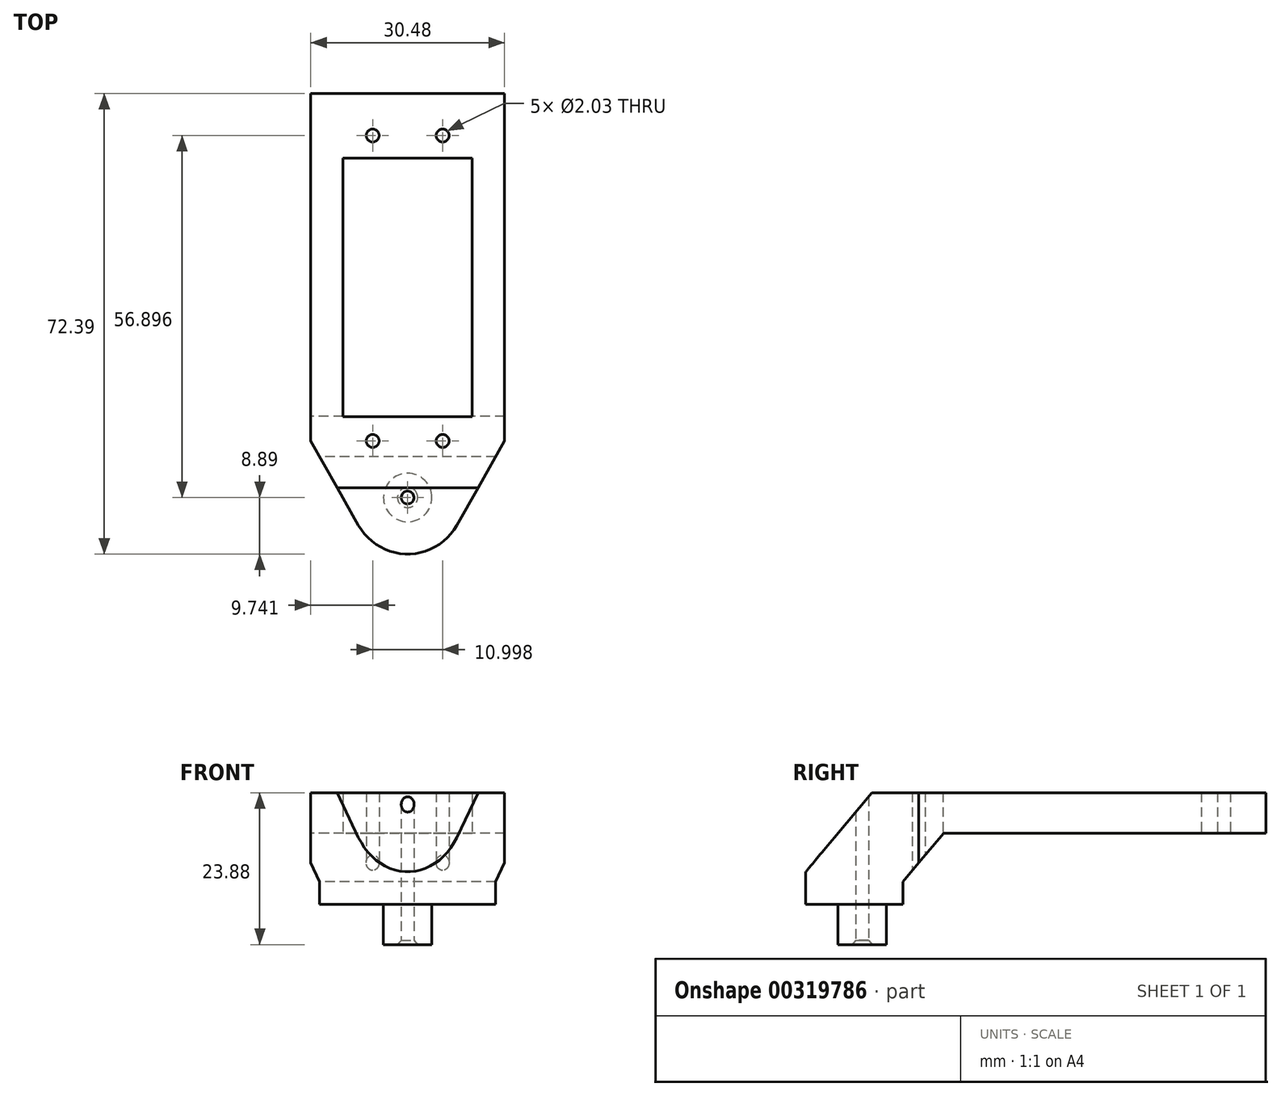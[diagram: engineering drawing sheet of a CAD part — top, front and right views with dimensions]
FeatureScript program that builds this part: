
annotation { "Feature Type Name" : "Feature", "Feature Type Description" : "" }
export const myFeature = defineFeature(function(context is Context, id is Id, definition is map)
    precondition{}
    {
        {
            var Q0;
            Q0=qCreatedBy(makeId("Top.planeOp"),FACE);
            var sketch = newSketch(context, id + "F0", { "sketchPlane" : qUnion([Q0])});
            skLineSegment(sketch, "E0", {"start": v(0, -10.16) * mm, "end": v(-10.16, -10.16) * mm});
            skLineSegment(sketch, "E1", {"start": v(-10.16, -10.16) * mm, "end": v(-10.16, 30.48) * mm});
            skLineSegment(sketch, "E2", {"start": v(-10.16, 30.48) * mm, "end": v(0, 30.48) * mm});
            skLineSegment(sketch, "E3", {"start": v(0, 40.64) * mm, "end": v(-15.24, 40.64) * mm});
            skLineSegment(sketch, "E4", {"start": v(-15.24, 40.64) * mm, "end": v(-15.24, -13.97) * mm});
            skLineSegment(sketch, "E5", {"start": v(-15.24, -13.97) * mm, "end": v(0, -13.97) * mm, "construction": true});
            skPoint(sketch, "E6", {"position": v(-5.5, -13.97) * mm});
            skCircle(sketch, "E7", {"center": v(0, 0) * mm, "radius": 6.35 * mm, "construction": true});
            skCircle(sketch, "E8", {"center": v(-5.5, -13.97) * mm, "radius": 1.02 * mm});
            skCircle(sketch, "E9", {"center": v(0, -22.86) * mm, "radius": 3.81 * mm, "construction": true});
            skCircle(sketch, "E10", {"center": v(-5.5, 34.04) * mm, "radius": 1.02 * mm});
            skCircle(sketch, "E11.MirrorC", {"center": v(5.5, -13.97) * mm, "radius": 1.02 * mm});
            skCircle(sketch, "E12.MirrorC", {"center": v(5.5, 34.04) * mm, "radius": 1.02 * mm});
            skLineSegment(sketch, "E13.MirrorCS", {"start": v(15.24, -13.97) * mm, "end": v(0, -13.97) * mm, "construction": true});
            skLineSegment(sketch, "E14.MirrorCS", {"start": v(15.24, 40.64) * mm, "end": v(15.24, -13.97) * mm});
            skLineSegment(sketch, "E15.MirrorCS", {"start": v(0, -10.16) * mm, "end": v(10.16, -10.16) * mm});
            skLineSegment(sketch, "E16.MirrorCS", {"start": v(10.16, 30.48) * mm, "end": v(0, 30.48) * mm});
            skLineSegment(sketch, "E17.MirrorCS", {"start": v(10.16, -10.16) * mm, "end": v(10.16, 30.48) * mm});
            skLineSegment(sketch, "E18.MirrorCS", {"start": v(0, 40.64) * mm, "end": v(15.24, 40.64) * mm});
            skCircle(sketch, "E19", {"center": v(0, -22.86) * mm, "radius": 8.9 * mm});
            skLineSegment(sketch, "E20", {"start": v(-15.24, -13.97) * mm, "end": v(-7.74, -27.24) * mm});
            skLineSegment(sketch, "E21", {"start": v(15.24, -13.97) * mm, "end": v(7.74, -27.24) * mm});
            skSolve(sketch);
        }
        {
            var Q0;
            Q0 = qSketchRegion(id + "F0", true);
            extrude(context, id + "F1", {"entities" : qUnion([Q0]), "depth" : 17.53 * mm});
        }
        {
            var Q0;
            Q0=qCreatedBy(makeId("Right.planeOp"),FACE);
            var sketch = newSketch(context, id + "F2", { "sketchPlane" : qUnion([Q0])});
            skLineSegment(sketch, "E22", {"start": v(-31.76, 0) * mm, "end": v(-31.76, 5.08) * mm});
            skLineSegment(sketch, "E23", {"start": v(-31.76, 5.08) * mm, "end": v(-21.32, 17.53) * mm});
            skLineSegment(sketch, "E24", {"start": v(-21.32, 17.53) * mm, "end": v(41.78, 17.53) * mm});
            skLineSegment(sketch, "E25", {"start": v(41.78, 17.53) * mm, "end": v(41.78, 11.18) * mm});
            skLineSegment(sketch, "E26", {"start": v(41.78, 11.18) * mm, "end": v(-10.07, 11.18) * mm});
            skLineSegment(sketch, "E27", {"start": v(-10.07, 11.18) * mm, "end": v(-16.46, 3.56) * mm});
            skLineSegment(sketch, "E28", {"start": v(-16.46, 3.56) * mm, "end": v(-16.46, 0) * mm});
            skLineSegment(sketch, "E29", {"start": v(-16.46, 0) * mm, "end": v(-31.76, 0) * mm});
            skSolve(sketch);
        }
        {
            var Q0;
            Q0 = qSketchRegion(id + "F2", true);
            extrude(context, id + "F3", {"entities" : qUnion([Q0]), "operationType" : NewBodyOperationType.INTERSECT, "endBound" : BoundingType.THROUGH_ALL, "depth" : 25.4 * mm, "hasSecondDirection" : true, "secondDirectionOppositeDirection" : true, "secondDirectionDepth" : 25.4 * mm});
        }
        {
            var Q0;
            Q0=qCreatedBy(makeId("Top.planeOp"),FACE);
            var sketch = newSketch(context, id + "F4", { "sketchPlane" : qUnion([Q0])});
            skCircle(sketch, "E30", {"center": v(0, -22.86) * mm, "radius": 3.81 * mm});
            skSolve(sketch);
        }
        {
            var Q0;
            Q0 = qSketchRegion(id + "F4", true);
            extrude(context, id + "F5", {"entities" : qUnion([Q0]), "operationType" : NewBodyOperationType.ADD, "oppositeDirection" : true, "depth" : 6.35 * mm});
        }
        {
            var Q0;
            Q0=makeQuery(id+"F5.opExtrude","CAP_FACE",FACE,{"disambiguationData":[OSD([sQuery(id+"F4.wireOp",EDGE,"E30")])],"isStart":false});
            var sketch = newSketch(context, id + "F6", { "sketchPlane" : qUnion([Q0])});
            skPoint(sketch, "E31", {"position": v(0, 22.86) * mm});
            skSolve(sketch);
        }
        {
            var Q0;
            Q0=sQuery(id+"F6.wireOp",VERTEX,"E31");
            var Q1;
            Q1=makeQuery(id+"F1.opExtrude","SWEPT_BODY",BODY,{"disambiguationData":[OSD([sQuery(id+"F0.wireOp",EDGE,"E0"),sQuery(id+"F0.wireOp",EDGE,"E1"),sQuery(id+"F0.wireOp",EDGE,"E2"),sQuery(id+"F0.wireOp",EDGE,"E3"),sQuery(id+"F0.wireOp",EDGE,"E4"),sQuery(id+"F0.wireOp",EDGE,"E8"),sQuery(id+"F0.wireOp",EDGE,"E10"),sQuery(id+"F0.wireOp",EDGE,"E11.MirrorC"),sQuery(id+"F0.wireOp",EDGE,"E12.MirrorC"),sQuery(id+"F0.wireOp",EDGE,"E14.MirrorCS"),sQuery(id+"F0.wireOp",EDGE,"E15.MirrorCS"),sQuery(id+"F0.wireOp",EDGE,"E16.MirrorCS"),sQuery(id+"F0.wireOp",EDGE,"E17.MirrorCS"),sQuery(id+"F0.wireOp",EDGE,"E18.MirrorCS"),sQuery(id+"F0.wireOp",EDGE,"E19"),sQuery(id+"F0.wireOp",EDGE,"E20"),sQuery(id+"F0.wireOp",EDGE,"E21")])]});
            hole(context, id + "F7", {"style" : HoleStyle.C_SINK, "endStyle" : HoleEndStyle.THROUGH, "holeDiameter" : 2.03 * mm, "cSinkDiameter" : 3.17 * mm, "cSinkAngle" : 82 * degree, "tappedDepth" : 12.7 * mm, "tapClearance" : 3, "locations" : qUnion([Q0]), "scope" : qUnion([Q1])});
        }
    });
